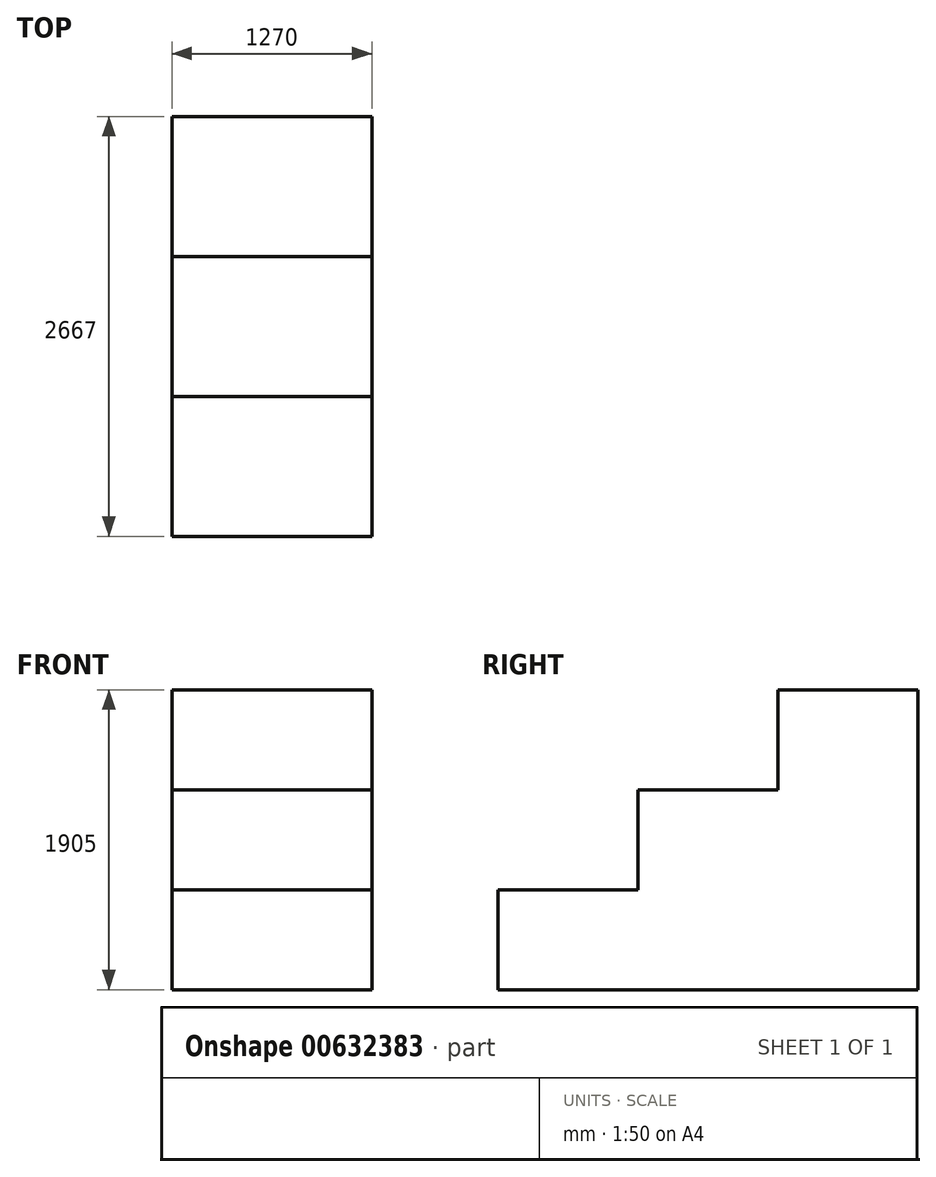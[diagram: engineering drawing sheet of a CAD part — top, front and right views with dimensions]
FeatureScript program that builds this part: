
annotation { "Feature Type Name" : "Feature", "Feature Type Description" : "" }
export const myFeature = defineFeature(function(context is Context, id is Id, definition is map)
    precondition{}
    {
        {
            var Q0;
            Q0=qCreatedBy(makeId("Right.planeOp"),FACE);
            var sketch = newSketch(context, id + "F0", { "sketchPlane" : qUnion([Q0])});
            skLineSegment(sketch, "E0", {"start": v(-51.28, -45.92) * mm, "end": v(2615.72, -45.92) * mm});
            skLineSegment(sketch, "E1", {"start": v(2615.72, -45.92) * mm, "end": v(2615.72, 1859.08) * mm});
            skLineSegment(sketch, "E2", {"start": v(2615.72, 1859.08) * mm, "end": v(1726.72, 1859.08) * mm});
            skLineSegment(sketch, "E3", {"start": v(1726.72, 1859.08) * mm, "end": v(1726.72, 1224.08) * mm});
            skLineSegment(sketch, "E4", {"start": v(1726.72, 1224.08) * mm, "end": v(837.72, 1224.08) * mm});
            skLineSegment(sketch, "E5", {"start": v(837.72, 1224.08) * mm, "end": v(837.72, 589.08) * mm});
            skLineSegment(sketch, "E6", {"start": v(837.72, 589.08) * mm, "end": v(-51.28, 589.08) * mm});
            skLineSegment(sketch, "E7", {"start": v(-51.28, 589.08) * mm, "end": v(-51.28, -45.92) * mm});
            skSolve(sketch);
        }
        {
            var Q0;
            Q0 = qSketchRegion(id + "F0", true);
            extrude(context, id + "F1", {"entities" : qUnion([Q0]), "depth" : 1270 * mm, "offsetDistance" : 25.4 * mm});
        }
    });
